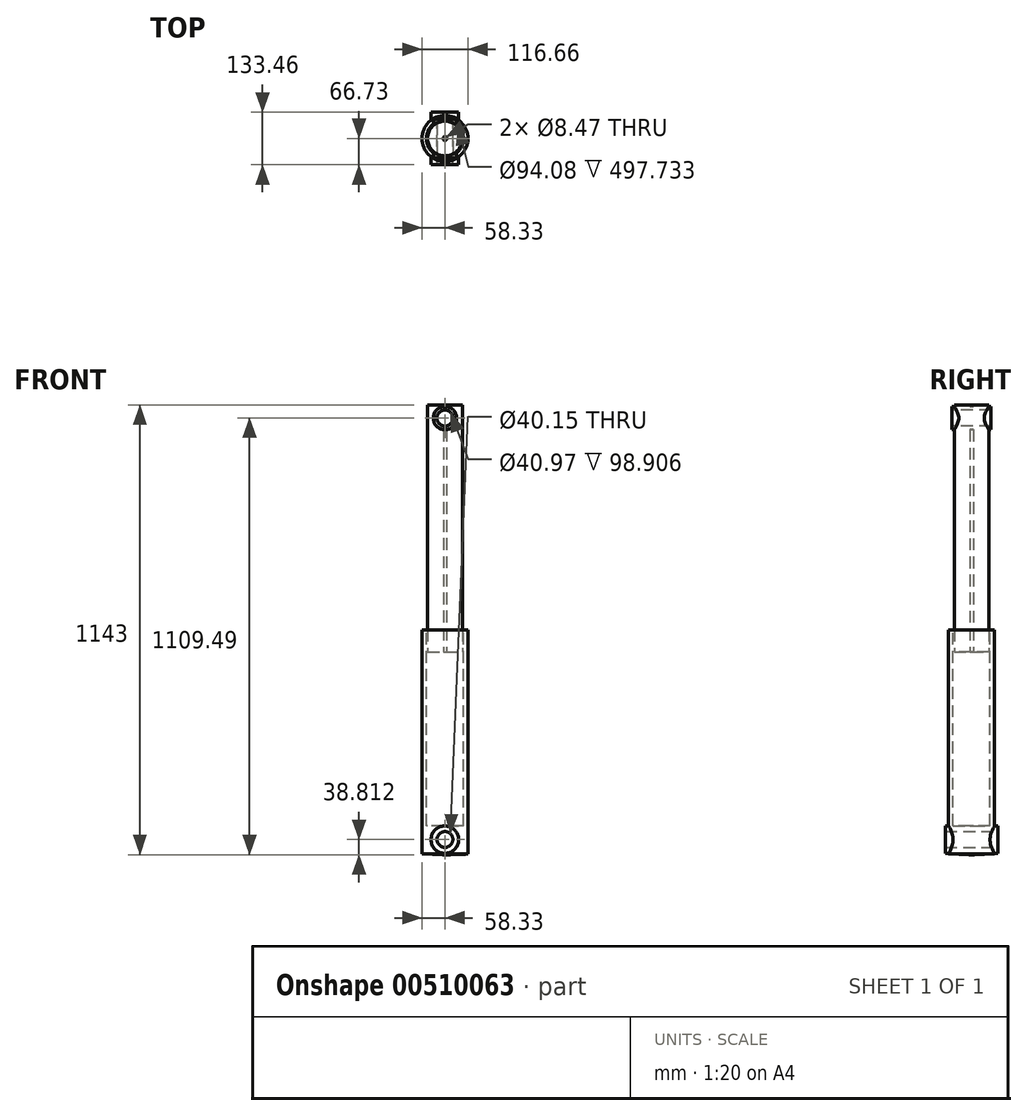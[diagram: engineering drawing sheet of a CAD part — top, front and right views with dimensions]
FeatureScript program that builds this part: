
annotation { "Feature Type Name" : "Feature", "Feature Type Description" : "" }
export const myFeature = defineFeature(function(context is Context, id is Id, definition is map)
    precondition{}
    {
        {
            var Q0;
            Q0=qCreatedBy(makeId("Front.planeOp"),FACE);
            var sketch = newSketch(context, id + "F0", { "sketchPlane" : qUnion([Q0])});
            skLineSegment(sketch, "E0", {"start": v(0, 0) * mm, "end": v(0, 571.5) * mm, "construction": true});
            skLineSegment(sketch, "E1", {"start": v(0, 0) * mm, "end": v(0, -571.5) * mm, "construction": true});
            skLineSegment(sketch, "E2", {"start": v(0, 571.5) * mm, "end": v(44.09, 571.5) * mm});
            skLineSegment(sketch, "E3", {"start": v(44.09, 571.5) * mm, "end": v(44.09, -55.9) * mm});
            skLineSegment(sketch, "E4", {"start": v(44.09, -55.9) * mm, "end": v(0, -55.9) * mm});
            skLineSegment(sketch, "E5", {"start": v(4.24, -55.9) * mm, "end": v(4.24, 571.5) * mm});
            skLineSegment(sketch, "E6", {"start": v(47.04, 0) * mm, "end": v(47.04, -497.73) * mm});
            skLineSegment(sketch, "E7", {"start": v(47.04, -497.73) * mm, "end": v(4.04, -497.77) * mm});
            skLineSegment(sketch, "E8", {"start": v(4.04, -497.77) * mm, "end": v(6.74, -571.5) * mm});
            skLineSegment(sketch, "E9", {"start": v(6.74, -571.5) * mm, "end": v(58.33, -569.79) * mm});
            skLineSegment(sketch, "E10", {"start": v(58.33, -569.79) * mm, "end": v(58.33, 0) * mm});
            skLineSegment(sketch, "E11", {"start": v(58.33, 0) * mm, "end": v(47.04, 0) * mm});
            skSolve(sketch);
        }
        {
            var Q0;
            {var subQ0=sQuery(id+"F0.wireOp",EDGE,"E3");Q0=makeQuery(id+"F0.imprint","IMPRINT",FACE,{"disambiguationData":[TD([[makeQuery(id+"F0.imprint","IMPRINT",EDGE,{"derivedFrom":subQ0}),-1.0]])]});}
            var Q1;
            Q1=sQuery(id+"F0.wireOp",EDGE,"E0");
            revolve(context, id + "F1", {"entities" : qUnion([Q0]), "axis" : qUnion([Q1]), "revolveType" : RevolveType.FULL});
        }
        {
            var Q0;
            Q0=makeQuery(id+"F0.imprint","IMPRINT",FACE,{"disambiguationData":[TD([[makeQuery(id+"F0.imprint","IMPRINT",EDGE,{"derivedFrom":sQuery(id+"F0.wireOp",EDGE,"E6")}),1.0]])]});
            var Q1;
            Q1=sQuery(id+"F0.wireOp",EDGE,"E1");
            revolve(context, id + "F2", {"entities" : qUnion([Q0]), "axis" : qUnion([Q1]), "revolveType" : RevolveType.FULL});
        }
        {
            var Q0;
            Q0=qCreatedBy(makeId("Front.planeOp"),FACE);
            var sketch = newSketch(context, id + "F3", { "sketchPlane" : qUnion([Q0])});
            skCircle(sketch, "E12", {"center": v(0, -532.69) * mm, "radius": 20.07 * mm});
            skSolve(sketch);
        }
        {
            var Q0;
            Q0=qCreatedBy(makeId("Front.planeOp"),FACE);
            var sketch = newSketch(context, id + "F4", { "sketchPlane" : qUnion([Q0])});
            skCircle(sketch, "E13", {"center": v(-0.32, -533.24) * mm, "radius": 34.9 * mm});
            skSolve(sketch);
        }
        {
            var Q0;
            Q0 = qSketchRegion(id + "F4", true);
            extrude(context, id + "F5", {"entities" : qUnion([Q0]), "operationType" : NewBodyOperationType.ADD, "endBound" : BoundingType.SYMMETRIC, "depth" : 133.47 * mm, "offsetDistance" : 25.4 * mm});
        }
        {
            var Q0;
            Q0 = qSketchRegion(id + "F3", true);
            extrude(context, id + "F6", {"entities" : qUnion([Q0]), "operationType" : NewBodyOperationType.REMOVE, "endBound" : BoundingType.SYMMETRIC, "depth" : 300.95 * mm, "offsetDistance" : 25.4 * mm});
        }
        {
            var Q0;
            Q0=qCreatedBy(makeId("Front.planeOp"),FACE);
            var sketch = newSketch(context, id + "F7", { "sketchPlane" : qUnion([Q0])});
            skCircle(sketch, "E14", {"center": v(0, 538) * mm, "radius": 29.68 * mm});
            skSolve(sketch);
        }
        {
            var Q0;
            Q0 = qSketchRegion(id + "F7", true);
            var Q1;
            Q1=sQuery(id+"F7.wireOp",EDGE,"E14");
            extrude(context, id + "F8", {"entities" : qUnion([Q0]), "operationType" : NewBodyOperationType.ADD, "surfaceEntities" : qUnion([Q1]), "endBound" : BoundingType.SYMMETRIC, "depth" : 98.9 * mm, "offsetDistance" : 25.4 * mm});
        }
        {
            var Q0;
            Q0=makeQuery(id+"F8.opExtrude","CAP_FACE",FACE,{"disambiguationData":[OSD([sQuery(id+"F7.wireOp",EDGE,"E14")])],"isStart":false});
            var sketch = newSketch(context, id + "F9", { "sketchPlane" : qUnion([Q0])});
            skCircle(sketch, "E15", {"center": v(0, 538) * mm, "radius": 20.48 * mm});
            skSolve(sketch);
        }
        {
            var Q0;
            Q0=makeQuery(id+"F9.imprint","IMPRINT",FACE,{"disambiguationData":[TD([[makeQuery(id+"F9.imprint","IMPRINT",EDGE,{"derivedFrom":sQuery(id+"F9.wireOp",EDGE,"E15")}),1.0]])]});
            var Q1;
            Q1=sQuery(id+"F9.wireOp",EDGE,"E15");
            extrude(context, id + "F10", {"entities" : qUnion([Q0]), "operationType" : NewBodyOperationType.REMOVE, "surfaceEntities" : qUnion([Q1]), "oppositeDirection" : true, "depth" : 250.86 * mm, "offsetDistance" : 25.4 * mm});
        }
    });
